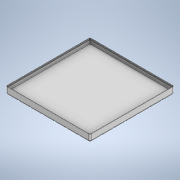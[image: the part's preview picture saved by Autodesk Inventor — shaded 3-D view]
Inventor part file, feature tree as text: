
AUTODESK INVENTOR PART (.ipt)
format: ipt  version: 2022.3 (Build 263350000, 350)  size: 1,472,000 bytes
history: native  units: mm
features: sketch x7, extrude x7, sweep x3, projected_geometry x2, plane x1, draft x1, pattern_linear x1, fillet x1
ambient origin geometry x8: Origin, YZ Plane, XZ Plane, XY Plane, X Axis, Y Axis, Z Axis, Center Point
bodies: Solid1 (feature_tree)
feature tree (23):
  sketch  "Sketch1"  dims[d0=42.0mm d1=42.0mm]
  extrude  "Extrusion1"  Depth=42.0mm
  plane  "Work Plane1"
  sweep  "Sweep1"
  extrude  "Extrusion2"  Depth=6.5mm
  draft  "FaceDraft1"
  extrude  "Extrusion3"  TaperAngle=0.0deg  [1 undecoded]
  extrude  "Extrusion4"  Depth=2.4mm
  pattern_linear  "Rectangular Pattern1"  Spacing1=4.0mm  [1 undecoded]
  sketch  "Sketch4"  dims[d6=5.0mm d7=0.0mm]
  extrude  "Extrusion5"  TaperAngle=0.0deg  [1 undecoded]
  sweep  "Sweep2"
  extrude  "Extrusion6"  TaperAngle=0.0deg  [1 undecoded]
  fillet  "Fillet1"  [1 undecoded]
  extrude  "Extrusion7"  Depth=1.2mm
  sweep  "Sweep3"
  sketch  "Sketch2"  dims[d2=13.0mm d3=8.0mm]
  projected_geometry  "Projected Loop1"
  sketch  "Sketch3"  dims[d4=3.0mm d5=6.5mm]
  sketch  "Sketch5"  dims[d8=45.0deg d9=2.4mm]
  sketch  "Sketch6"  dims[d10=45.0deg]
  projected_geometry  "Projected Loop2"
  sketch  "Sketch7"  dims[d11=0.8mm d12=4.0mm d13=0.0mm d14=0.0mm d15=4.0mm d16=0.0mm d17=15.0deg d18=4.0mm d19=0.0mm d20=2.4mm d21=0.0mm d22=70.0mm d24=42.0mm d25=70.0mm d27=42.0mm d28=294.0mm d29=294.0mm d30=4.0mm d31=16.0mm d32=0.0mm d33=5.0mm d36=45.0deg d37=0.8mm d38=45.0deg d39=0.25mm d40=0.0mm d41=0.0mm d42=0.25mm d43=0.0mm d44=0.0mm d45=0.6mm d47=2.4mm d48=14.8mm d49=0.0mm d50=45.0deg d51=1.2mm d52=1.2mm d53=0.0mm d54=0.0mm]
note: 5 required parameter values undecoded (feature->parameter linkage not recoverable at this tier; creation-order binding heuristic only, values carry confidence <= 0.55)
